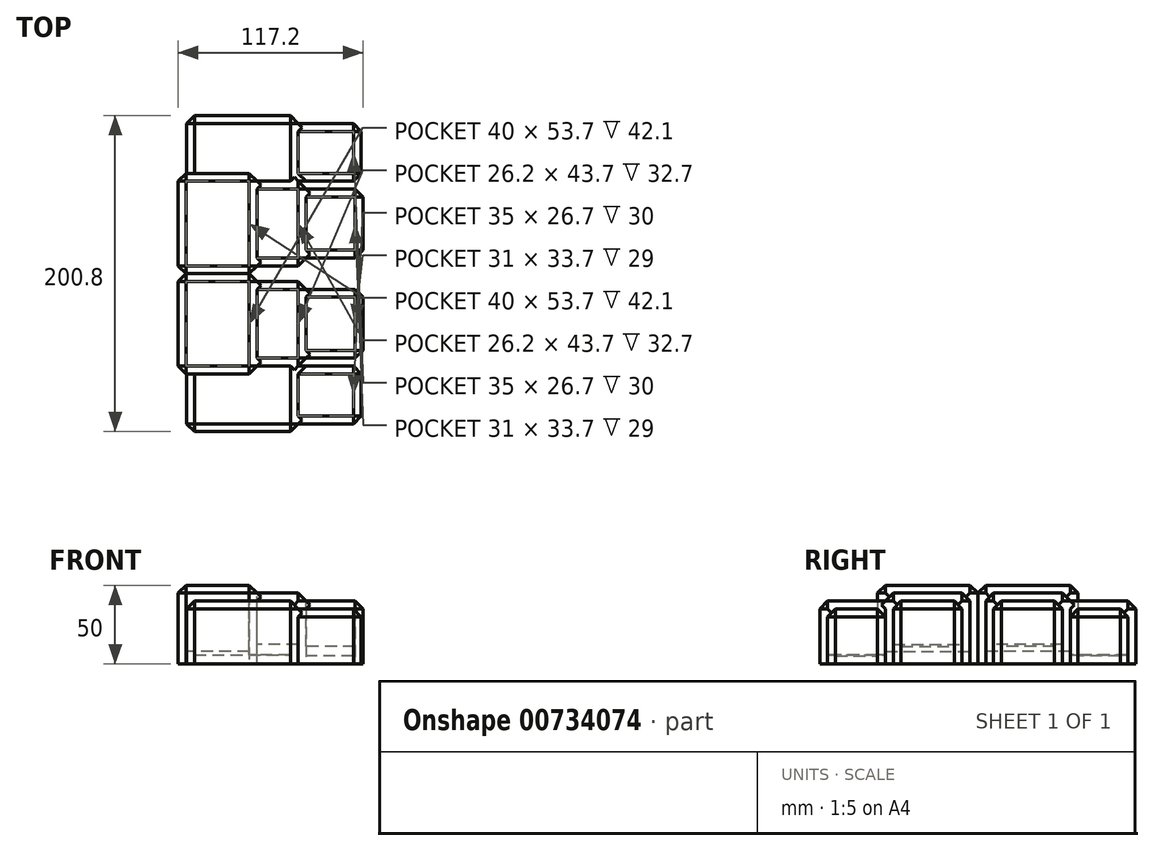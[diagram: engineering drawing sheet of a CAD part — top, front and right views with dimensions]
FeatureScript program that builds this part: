
annotation { "Feature Type Name" : "Feature", "Feature Type Description" : "" }
export const myFeature = defineFeature(function(context is Context, id is Id, definition is map)
    precondition{}
    {
        {
            var Q0;
            Q0=qCreatedBy(makeId("Front.planeOp"),FACE);
            var sketch = newSketch(context, id + "F0", { "sketchPlane" : qUnion([Q0])});
            skLineSegment(sketch, "E0.bottom", {"start": v(-30.12, 38) * mm, "end": v(19.88, 38) * mm});
            skLineSegment(sketch, "E0.top", {"start": v(-30.12, -12) * mm, "end": v(19.88, -12) * mm});
            skLineSegment(sketch, "E0.left", {"start": v(-30.12, 38) * mm, "end": v(-30.12, -12) * mm});
            skLineSegment(sketch, "E0.right", {"start": v(19.88, 38) * mm, "end": v(19.88, -12) * mm});
            skSolve(sketch);
        }
        {
            var Q0;
            Q0 = qSketchRegion(id + "F0", true);
            extrude(context, id + "F1", {"entities" : qUnion([Q0]), "depth" : 63.7 * mm, "offsetDistance" : 25 * mm});
        }
        {
            var Q0;
            Q0=makeQuery(id+"F1.opExtrude","CAP_EDGE",EDGE,{"disambiguationData":[OSD([sQuery(id+"F0.wireOp",EDGE,"E0.right")])],"isStart":false});
            var Q1;
            Q1=makeQuery(id+"F1.opExtrude","CAP_EDGE",EDGE,{"disambiguationData":[OSD([sQuery(id+"F0.wireOp",EDGE,"E0.bottom")])],"isStart":false});
            var Q2;
            Q2=makeQuery(id+"F1.opExtrude","CAP_EDGE",EDGE,{"disambiguationData":[OSD([sQuery(id+"F0.wireOp",EDGE,"E0.left")])],"isStart":false});
            var Q3;
            Q3=makeQuery(id+"F1.opExtrude","SWEPT_EDGE",EDGE,{"disambiguationData":[OSD([sQuery(id+"F0.wireOp",EDGE,"E0.bottom"),sQuery(id+"F0.wireOp",EDGE,"E0.right")])]});
            var Q4;
            Q4=makeQuery(id+"F1.opExtrude","SWEPT_EDGE",EDGE,{"disambiguationData":[OSD([sQuery(id+"F0.wireOp",EDGE,"E0.bottom"),sQuery(id+"F0.wireOp",EDGE,"E0.left")])]});
            var Q5;
            Q5=makeQuery(id+"F1.opExtrude","CAP_EDGE",EDGE,{"disambiguationData":[OSD([sQuery(id+"F0.wireOp",EDGE,"E0.right")])],"isStart":true});
            var Q6;
            Q6=makeQuery(id+"F1.opExtrude","CAP_EDGE",EDGE,{"disambiguationData":[OSD([sQuery(id+"F0.wireOp",EDGE,"E0.bottom")])],"isStart":true});
            var Q7;
            Q7=makeQuery(id+"F1.opExtrude","CAP_EDGE",EDGE,{"disambiguationData":[OSD([sQuery(id+"F0.wireOp",EDGE,"E0.left")])],"isStart":true});
            chamfer(context, id + "F2", {"entities" : qUnion([Q0, Q1, Q2, Q3, Q4, Q5, Q6, Q7]), "width" : 5 * mm, "tangentPropagation" : true});
        }
        {
            var Q0;
            Q0=makeQuery(id+"F1.opExtrude","SWEPT_FACE",FACE,{"disambiguationData":[OSD([sQuery(id+"F0.wireOp",EDGE,"E0.bottom")])]});
            extrude(context, id + "F3", {"entities" : qUnion([Q0]), "operationType" : NewBodyOperationType.REMOVE, "oppositeDirection" : true, "depth" : 42.1 * mm, "offsetDistance" : 25 * mm});
        }
        {
            var Q0;
            Q0=makeQuery(id+"F1.opExtrude","SWEPT_FACE",FACE,{"disambiguationData":[OSD([sQuery(id+"F0.wireOp",EDGE,"E0.right")])]});
            extrude(context, id + "F4", {"entities" : qUnion([Q0]), "operationType" : NewBodyOperationType.ADD, "depth" : 31.2 * mm, "offsetDistance" : 25 * mm});
        }
        {
            var Q0;
            {var subQ0=sQuery(id+"F0.wireOp",EDGE,"E0.right");var subQ1=sQuery(id+"F0.wireOp",EDGE,"E0.bottom");Q0=makeQuery(id+"F4.opExtrude","SWEPT_EDGE",EDGE,{"disambiguationData":[OSD([subQ1,subQ0]),TDD([makeQuery(id+"F2.opChamfer","BLEND_VERTEX",VERTEX,{"blendedFrom":[makeQuery(id+"F1.opExtrude","CAP_VERTEX",VERTEX,{"disambiguationData":[OSD([subQ1,subQ0])],"isStart":false}),makeQuery(id+"F1.opExtrude","SWEPT_EDGE",EDGE,{"disambiguationData":[OSD([subQ1,subQ0])]}),makeQuery(id+"F1.opExtrude","CAP_EDGE",EDGE,{"disambiguationData":[OSD([subQ0])],"isStart":false}),makeQuery(id+"F1.opExtrude","SWEPT_FACE",FACE,{"disambiguationData":[OSD([subQ0])]})],"blendedInto":[makeQuery(id+"F1.opExtrude","SWEPT_FACE",FACE,{"disambiguationData":[OSD([subQ0])]})]})])]});}
            var Q1;
            {var subQ0=sQuery(id+"F0.wireOp",EDGE,"E0.right");var subQ1=sQuery(id+"F0.wireOp",EDGE,"E0.bottom");Q1=makeQuery(id+"F4.opExtrude","SWEPT_EDGE",EDGE,{"disambiguationData":[OSD([subQ1,subQ0]),TDD([makeQuery(id+"F2.opChamfer","BLEND_VERTEX",VERTEX,{"blendedFrom":[makeQuery(id+"F1.opExtrude","CAP_VERTEX",VERTEX,{"disambiguationData":[OSD([subQ1,subQ0])],"isStart":true}),makeQuery(id+"F1.opExtrude","SWEPT_EDGE",EDGE,{"disambiguationData":[OSD([subQ1,subQ0])]}),makeQuery(id+"F1.opExtrude","CAP_EDGE",EDGE,{"disambiguationData":[OSD([subQ0])],"isStart":true}),makeQuery(id+"F1.opExtrude","SWEPT_FACE",FACE,{"disambiguationData":[OSD([subQ0])]})],"blendedInto":[makeQuery(id+"F1.opExtrude","SWEPT_FACE",FACE,{"disambiguationData":[OSD([subQ0])]})]})])]});}
            var Q2;
            Q2=makeQuery(id+"F4.opExtrude","CAP_EDGE",EDGE,{"disambiguationData":[OSD([sQuery(id+"F0.wireOp",EDGE,"E0.bottom"),sQuery(id+"F0.wireOp",EDGE,"E0.right")])],"isStart":false});
            var Q3;
            {var subQ0=sQuery(id+"F0.wireOp",EDGE,"E0.right");Q3=makeQuery(id+"F4.opExtrude","CAP_EDGE",EDGE,{"disambiguationData":[OSD([subQ0]),TDD([makeQuery(id+"F2.opChamfer","BLEND_EDGE",EDGE,{"blendedFrom":[makeQuery(id+"F1.opExtrude","CAP_EDGE",EDGE,{"disambiguationData":[OSD([subQ0])],"isStart":false}),makeQuery(id+"F1.opExtrude","SWEPT_FACE",FACE,{"disambiguationData":[OSD([subQ0])]})],"blendedInto":[makeQuery(id+"F1.opExtrude","SWEPT_FACE",FACE,{"disambiguationData":[OSD([subQ0])]})]})])],"isStart":false});}
            var Q4;
            {var subQ0=sQuery(id+"F0.wireOp",EDGE,"E0.right");Q4=makeQuery(id+"F4.opExtrude","CAP_EDGE",EDGE,{"disambiguationData":[OSD([subQ0]),TDD([makeQuery(id+"F2.opChamfer","BLEND_EDGE",EDGE,{"blendedFrom":[makeQuery(id+"F1.opExtrude","CAP_EDGE",EDGE,{"disambiguationData":[OSD([subQ0])],"isStart":true}),makeQuery(id+"F1.opExtrude","SWEPT_FACE",FACE,{"disambiguationData":[OSD([subQ0])]})],"blendedInto":[makeQuery(id+"F1.opExtrude","SWEPT_FACE",FACE,{"disambiguationData":[OSD([subQ0])]})]})])],"isStart":false});}
            chamfer(context, id + "F5", {"entities" : qUnion([Q0, Q1, Q2, Q3, Q4]), "width" : 5 * mm, "tangentPropagation" : true});
        }
        {
            var Q0;
            Q0=makeQuery(id+"F4.opExtrude","SWEPT_FACE",FACE,{"disambiguationData":[OSD([sQuery(id+"F0.wireOp",EDGE,"E0.bottom"),sQuery(id+"F0.wireOp",EDGE,"E0.right")])]});
            extrude(context, id + "F6", {"entities" : qUnion([Q0]), "operationType" : NewBodyOperationType.REMOVE, "oppositeDirection" : true, "depth" : 32.7 * mm, "offsetDistance" : 25 * mm});
        }
        {
            var Q0;
            {var subQ0=sQuery(id+"F0.wireOp",EDGE,"E0.right");Q0=makeQuery(id+"F4.opExtrude","SWEPT_FACE",FACE,{"disambiguationData":[OSD([subQ0]),TDD([makeQuery(id+"F2.opChamfer","BLEND_EDGE",EDGE,{"blendedFrom":[makeQuery(id+"F1.opExtrude","CAP_EDGE",EDGE,{"disambiguationData":[OSD([subQ0])],"isStart":false}),makeQuery(id+"F1.opExtrude","SWEPT_FACE",FACE,{"disambiguationData":[OSD([subQ0])]})],"blendedInto":[makeQuery(id+"F1.opExtrude","SWEPT_FACE",FACE,{"disambiguationData":[OSD([subQ0])]})]})])]});}
            extrude(context, id + "F7", {"entities" : qUnion([Q0]), "operationType" : NewBodyOperationType.ADD, "depth" : 41.7 * mm, "offsetDistance" : 25 * mm});
        }
        {
            var Q0;
            {var subQ0=sQuery(id+"F0.wireOp",EDGE,"E0.right");var subQ1=makeQuery(id+"F2.opChamfer","BLEND_EDGE",EDGE,{"blendedFrom":[makeQuery(id+"F1.opExtrude","CAP_EDGE",EDGE,{"disambiguationData":[OSD([subQ0])],"isStart":false}),makeQuery(id+"F1.opExtrude","SWEPT_FACE",FACE,{"disambiguationData":[OSD([subQ0])]})],"blendedInto":[makeQuery(id+"F1.opExtrude","SWEPT_FACE",FACE,{"disambiguationData":[OSD([subQ0])]})]});Q0=makeQuery(id+"F7.opExtrude","SWEPT_FACE",FACE,{"disambiguationData":[OSD([subQ0]),TDD([makeQuery(id+"F4.boolean.opBoolean","MERGE",EDGE,{"derivedFrom":[subQ1,makeQuery(id+"F4.opExtrude","CAP_EDGE",EDGE,{"disambiguationData":[OSD([subQ0]),TDD([subQ1])],"isStart":true})]})])]});}
            extrude(context, id + "F8", {"entities" : qUnion([Q0]), "operationType" : NewBodyOperationType.ADD, "depth" : 44.8 * mm, "offsetDistance" : 25 * mm});
        }
        {
            var Q0;
            Q0=makeQuery(id+"F8.opExtrude","CAP_EDGE",EDGE,{"disambiguationData":[OSD([sQuery(id+"F0.wireOp",EDGE,"E0.bottom"),sQuery(id+"F0.wireOp",EDGE,"E0.right")])],"isStart":false});
            var Q1;
            {var subQ0=sQuery(id+"F0.wireOp",EDGE,"E0.right");var subQ1=makeQuery(id+"F1.opExtrude","SWEPT_FACE",FACE,{"disambiguationData":[OSD([subQ0])]});var subQ2=makeQuery(id+"F1.opExtrude","CAP_EDGE",EDGE,{"disambiguationData":[OSD([subQ0])],"isStart":false});var subQ3=sQuery(id+"F0.wireOp",EDGE,"E0.bottom");Q1=makeQuery(id+"F8.boolean.opBoolean","MERGE",EDGE,{"derivedFrom":[makeQuery(id+"F7.opExtrude","CAP_EDGE",EDGE,{"disambiguationData":[OSD([subQ3,subQ0])],"isStart":false}),makeQuery(id+"F8.opExtrude","SWEPT_EDGE",EDGE,{"disambiguationData":[OSD([subQ3,subQ0]),TDD([makeQuery(id+"F7.opExtrude","CAP_VERTEX",VERTEX,{"disambiguationData":[OSD([subQ3,subQ0]),TDD([makeQuery(id+"F5.opChamfer","BLEND_VERTEX",VERTEX,{"blendedFrom":[makeQuery(id+"F4.opExtrude","SWEPT_EDGE",EDGE,{"disambiguationData":[OSD([subQ3,subQ0]),TDD([makeQuery(id+"F2.opChamfer","BLEND_VERTEX",VERTEX,{"blendedFrom":[makeQuery(id+"F1.opExtrude","CAP_VERTEX",VERTEX,{"disambiguationData":[OSD([subQ3,subQ0])],"isStart":false}),makeQuery(id+"F1.opExtrude","SWEPT_EDGE",EDGE,{"disambiguationData":[OSD([subQ3,subQ0])]}),subQ2,subQ1],"blendedInto":[subQ1]})])]}),makeQuery(id+"F2.opChamfer","BLEND_FACE",FACE,{"disambiguationData":[OSD([subQ0]),TDD([subQ2])]}),makeQuery(id+"F4.opExtrude","SWEPT_FACE",FACE,{"disambiguationData":[OSD([subQ0]),TDD([makeQuery(id+"F2.opChamfer","BLEND_EDGE",EDGE,{"blendedFrom":[subQ2,subQ1],"blendedInto":[subQ1]})])]})],"blendedInto":[makeQuery(id+"F2.opChamfer","BLEND_FACE",FACE,{"disambiguationData":[OSD([subQ0]),TDD([subQ2])]}),makeQuery(id+"F4.opExtrude","SWEPT_FACE",FACE,{"disambiguationData":[OSD([subQ0]),TDD([makeQuery(id+"F2.opChamfer","BLEND_EDGE",EDGE,{"blendedFrom":[subQ2,subQ1],"blendedInto":[subQ1]})])]})]})])],"isStart":false})])]})]});}
            var Q2;
            {var subQ0=sQuery(id+"F0.wireOp",EDGE,"E0.right");var subQ1=makeQuery(id+"F1.opExtrude","SWEPT_FACE",FACE,{"disambiguationData":[OSD([subQ0])]});var subQ2=makeQuery(id+"F1.opExtrude","CAP_EDGE",EDGE,{"disambiguationData":[OSD([subQ0])],"isStart":false});var subQ3=makeQuery(id+"F2.opChamfer","BLEND_EDGE",EDGE,{"blendedFrom":[subQ2,subQ1],"blendedInto":[subQ1]});var subQ4=sQuery(id+"F0.wireOp",EDGE,"E0.bottom");var subQ5=makeQuery(id+"F2.opChamfer","BLEND_VERTEX",VERTEX,{"blendedFrom":[makeQuery(id+"F1.opExtrude","CAP_VERTEX",VERTEX,{"disambiguationData":[OSD([subQ4,subQ0])],"isStart":false}),makeQuery(id+"F1.opExtrude","SWEPT_EDGE",EDGE,{"disambiguationData":[OSD([subQ4,subQ0])]}),subQ2,subQ1],"blendedInto":[subQ1]});Q2=makeQuery(id+"F7.opExtrude","SWEPT_EDGE",EDGE,{"disambiguationData":[OSD([subQ4,subQ0]),TDD([makeQuery(id+"F5.opChamfer","BLEND_VERTEX",VERTEX,{"blendedFrom":[makeQuery(id+"F4.opExtrude","CAP_VERTEX",VERTEX,{"disambiguationData":[OSD([subQ4,subQ0]),TDD([subQ5])],"isStart":false}),makeQuery(id+"F4.opExtrude","SWEPT_EDGE",EDGE,{"disambiguationData":[OSD([subQ4,subQ0]),TDD([subQ5])]}),makeQuery(id+"F4.opExtrude","CAP_EDGE",EDGE,{"disambiguationData":[OSD([subQ0]),TDD([subQ3])],"isStart":false}),makeQuery(id+"F4.opExtrude","SWEPT_FACE",FACE,{"disambiguationData":[OSD([subQ0]),TDD([subQ3])]})],"blendedInto":[makeQuery(id+"F4.opExtrude","SWEPT_FACE",FACE,{"disambiguationData":[OSD([subQ0]),TDD([subQ3])]})]})])]});}
            var Q3;
            {var subQ0=sQuery(id+"F0.wireOp",EDGE,"E0.right");var subQ1=makeQuery(id+"F2.opChamfer","BLEND_EDGE",EDGE,{"blendedFrom":[makeQuery(id+"F1.opExtrude","CAP_EDGE",EDGE,{"disambiguationData":[OSD([subQ0])],"isStart":false}),makeQuery(id+"F1.opExtrude","SWEPT_FACE",FACE,{"disambiguationData":[OSD([subQ0])]})],"blendedInto":[makeQuery(id+"F1.opExtrude","SWEPT_FACE",FACE,{"disambiguationData":[OSD([subQ0])]})]});Q3=makeQuery(id+"F7.opExtrude","CAP_EDGE",EDGE,{"disambiguationData":[OSD([subQ0]),TDD([makeQuery(id+"F5.opChamfer","BLEND_EDGE",EDGE,{"blendedFrom":[makeQuery(id+"F4.opExtrude","CAP_EDGE",EDGE,{"disambiguationData":[OSD([subQ0]),TDD([subQ1])],"isStart":false}),makeQuery(id+"F4.opExtrude","SWEPT_FACE",FACE,{"disambiguationData":[OSD([subQ0]),TDD([subQ1])]})],"blendedInto":[makeQuery(id+"F4.opExtrude","SWEPT_FACE",FACE,{"disambiguationData":[OSD([subQ0]),TDD([subQ1])]})]})])],"isStart":false});}
            var Q4;
            {var subQ0=sQuery(id+"F0.wireOp",EDGE,"E0.right");var subQ1=makeQuery(id+"F2.opChamfer","BLEND_EDGE",EDGE,{"blendedFrom":[makeQuery(id+"F1.opExtrude","CAP_EDGE",EDGE,{"disambiguationData":[OSD([subQ0])],"isStart":false}),makeQuery(id+"F1.opExtrude","SWEPT_FACE",FACE,{"disambiguationData":[OSD([subQ0])]})],"blendedInto":[makeQuery(id+"F1.opExtrude","SWEPT_FACE",FACE,{"disambiguationData":[OSD([subQ0])]})]});Q4=makeQuery(id+"F8.opExtrude","CAP_EDGE",EDGE,{"disambiguationData":[OSD([subQ0]),TDD([makeQuery(id+"F7.opExtrude","CAP_EDGE",EDGE,{"disambiguationData":[OSD([subQ0]),TDD([makeQuery(id+"F4.boolean.opBoolean","MERGE",EDGE,{"derivedFrom":[subQ1,makeQuery(id+"F4.opExtrude","CAP_EDGE",EDGE,{"disambiguationData":[OSD([subQ0]),TDD([subQ1])],"isStart":true})]})])],"isStart":false})])],"isStart":false});}
            chamfer(context, id + "F9", {"entities" : qUnion([Q0, Q1, Q2, Q3, Q4]), "width" : 5 * mm, "tangentPropagation" : true});
        }
        {
            var Q0;
            {var subQ0=sQuery(id+"F0.wireOp",EDGE,"E0.right");var subQ1=sQuery(id+"F0.wireOp",EDGE,"E0.bottom");Q0=makeQuery(id+"F8.boolean.opBoolean","MERGE",FACE,{"derivedFrom":[makeQuery(id+"F7.opExtrude","SWEPT_FACE",FACE,{"disambiguationData":[OSD([subQ1,subQ0])]}),makeQuery(id+"F8.opExtrude","SWEPT_FACE",FACE,{"disambiguationData":[OSD([subQ1,subQ0])]})]});}
            extrude(context, id + "F10", {"entities" : qUnion([Q0]), "operationType" : NewBodyOperationType.REMOVE, "oppositeDirection" : true, "depth" : 34.3 * mm, "offsetDistance" : 25 * mm});
        }
        {
            var Q0;
            {var subQ0=sQuery(id+"F0.wireOp",EDGE,"E0.right");var subQ1=makeQuery(id+"F2.opChamfer","BLEND_EDGE",EDGE,{"blendedFrom":[makeQuery(id+"F1.opExtrude","CAP_EDGE",EDGE,{"disambiguationData":[OSD([subQ0])],"isStart":false}),makeQuery(id+"F1.opExtrude","SWEPT_FACE",FACE,{"disambiguationData":[OSD([subQ0])]})],"blendedInto":[makeQuery(id+"F1.opExtrude","SWEPT_FACE",FACE,{"disambiguationData":[OSD([subQ0])]})]});Q0=makeQuery(id+"F7.opExtrude","SWEPT_FACE",FACE,{"disambiguationData":[OSD([subQ0]),TDD([makeQuery(id+"F5.opChamfer","BLEND_EDGE",EDGE,{"blendedFrom":[makeQuery(id+"F4.opExtrude","CAP_EDGE",EDGE,{"disambiguationData":[OSD([subQ0]),TDD([subQ1])],"isStart":false}),makeQuery(id+"F4.opExtrude","SWEPT_FACE",FACE,{"disambiguationData":[OSD([subQ0]),TDD([subQ1])]})],"blendedInto":[makeQuery(id+"F4.opExtrude","SWEPT_FACE",FACE,{"disambiguationData":[OSD([subQ0]),TDD([subQ1])]})]})])]});}
            extrude(context, id + "F11", {"entities" : qUnion([Q0]), "operationType" : NewBodyOperationType.ADD, "depth" : 40 * mm, "offsetDistance" : 25 * mm});
        }
        {
            var Q0;
            {var subQ0=sQuery(id+"F0.wireOp",EDGE,"E0.right");var subQ1=makeQuery(id+"F1.opExtrude","SWEPT_FACE",FACE,{"disambiguationData":[OSD([subQ0])]});var subQ2=makeQuery(id+"F1.opExtrude","CAP_EDGE",EDGE,{"disambiguationData":[OSD([subQ0])],"isStart":false});var subQ3=makeQuery(id+"F2.opChamfer","BLEND_EDGE",EDGE,{"blendedFrom":[subQ2,subQ1],"blendedInto":[subQ1]});var subQ4=makeQuery(id+"F4.opExtrude","SWEPT_FACE",FACE,{"disambiguationData":[OSD([subQ0]),TDD([subQ3])]});var subQ5=makeQuery(id+"F4.opExtrude","CAP_EDGE",EDGE,{"disambiguationData":[OSD([subQ0]),TDD([subQ3])],"isStart":false});var subQ6=makeQuery(id+"F5.opChamfer","BLEND_EDGE",EDGE,{"blendedFrom":[subQ5,subQ4],"blendedInto":[subQ4]});var subQ7=sQuery(id+"F0.wireOp",EDGE,"E0.bottom");var subQ8=makeQuery(id+"F2.opChamfer","BLEND_VERTEX",VERTEX,{"blendedFrom":[makeQuery(id+"F1.opExtrude","CAP_VERTEX",VERTEX,{"disambiguationData":[OSD([subQ7,subQ0])],"isStart":false}),makeQuery(id+"F1.opExtrude","SWEPT_EDGE",EDGE,{"disambiguationData":[OSD([subQ7,subQ0])]}),subQ2,subQ1],"blendedInto":[subQ1]});var subQ9=makeQuery(id+"F5.opChamfer","BLEND_VERTEX",VERTEX,{"blendedFrom":[makeQuery(id+"F4.opExtrude","CAP_VERTEX",VERTEX,{"disambiguationData":[OSD([subQ7,subQ0]),TDD([subQ8])],"isStart":false}),makeQuery(id+"F4.opExtrude","SWEPT_EDGE",EDGE,{"disambiguationData":[OSD([subQ7,subQ0]),TDD([subQ8])]}),subQ5,subQ4],"blendedInto":[subQ4]});Q0=makeQuery(id+"F11.opExtrude","SWEPT_EDGE",EDGE,{"disambiguationData":[OSD([subQ7,subQ0]),TDD([makeQuery(id+"F9.opChamfer","BLEND_VERTEX",VERTEX,{"blendedFrom":[makeQuery(id+"F7.opExtrude","CAP_VERTEX",VERTEX,{"disambiguationData":[OSD([subQ7,subQ0]),TDD([subQ9])],"isStart":false}),makeQuery(id+"F7.opExtrude","SWEPT_EDGE",EDGE,{"disambiguationData":[OSD([subQ7,subQ0]),TDD([subQ9])]}),makeQuery(id+"F7.opExtrude","CAP_EDGE",EDGE,{"disambiguationData":[OSD([subQ0]),TDD([subQ6])],"isStart":false}),makeQuery(id+"F7.opExtrude","SWEPT_FACE",FACE,{"disambiguationData":[OSD([subQ0]),TDD([subQ6])]})],"blendedInto":[makeQuery(id+"F7.opExtrude","SWEPT_FACE",FACE,{"disambiguationData":[OSD([subQ0]),TDD([subQ6])]})]})])]});}
            var Q1;
            {var subQ0=sQuery(id+"F0.wireOp",EDGE,"E0.right");var subQ1=makeQuery(id+"F2.opChamfer","BLEND_EDGE",EDGE,{"blendedFrom":[makeQuery(id+"F1.opExtrude","CAP_EDGE",EDGE,{"disambiguationData":[OSD([subQ0])],"isStart":false}),makeQuery(id+"F1.opExtrude","SWEPT_FACE",FACE,{"disambiguationData":[OSD([subQ0])]})],"blendedInto":[makeQuery(id+"F1.opExtrude","SWEPT_FACE",FACE,{"disambiguationData":[OSD([subQ0])]})]});var subQ2=makeQuery(id+"F5.opChamfer","BLEND_EDGE",EDGE,{"blendedFrom":[makeQuery(id+"F4.opExtrude","CAP_EDGE",EDGE,{"disambiguationData":[OSD([subQ0]),TDD([subQ1])],"isStart":false}),makeQuery(id+"F4.opExtrude","SWEPT_FACE",FACE,{"disambiguationData":[OSD([subQ0]),TDD([subQ1])]})],"blendedInto":[makeQuery(id+"F4.opExtrude","SWEPT_FACE",FACE,{"disambiguationData":[OSD([subQ0]),TDD([subQ1])]})]});Q1=makeQuery(id+"F11.opExtrude","CAP_EDGE",EDGE,{"disambiguationData":[OSD([subQ0]),TDD([makeQuery(id+"F9.opChamfer","BLEND_EDGE",EDGE,{"blendedFrom":[makeQuery(id+"F7.opExtrude","CAP_EDGE",EDGE,{"disambiguationData":[OSD([subQ0]),TDD([subQ2])],"isStart":false}),makeQuery(id+"F7.opExtrude","SWEPT_FACE",FACE,{"disambiguationData":[OSD([subQ0]),TDD([subQ2])]})],"blendedInto":[makeQuery(id+"F7.opExtrude","SWEPT_FACE",FACE,{"disambiguationData":[OSD([subQ0]),TDD([subQ2])]})]})])],"isStart":false});}
            var Q2;
            {var subQ0=sQuery(id+"F0.wireOp",EDGE,"E0.right");var subQ1=makeQuery(id+"F2.opChamfer","BLEND_EDGE",EDGE,{"blendedFrom":[makeQuery(id+"F1.opExtrude","CAP_EDGE",EDGE,{"disambiguationData":[OSD([subQ0])],"isStart":false}),makeQuery(id+"F1.opExtrude","SWEPT_FACE",FACE,{"disambiguationData":[OSD([subQ0])]})],"blendedInto":[makeQuery(id+"F1.opExtrude","SWEPT_FACE",FACE,{"disambiguationData":[OSD([subQ0])]})]});var subQ2=makeQuery(id+"F5.opChamfer","BLEND_EDGE",EDGE,{"blendedFrom":[makeQuery(id+"F4.opExtrude","CAP_EDGE",EDGE,{"disambiguationData":[OSD([subQ0]),TDD([subQ1])],"isStart":false}),makeQuery(id+"F4.opExtrude","SWEPT_FACE",FACE,{"disambiguationData":[OSD([subQ0]),TDD([subQ1])]})],"blendedInto":[makeQuery(id+"F4.opExtrude","SWEPT_FACE",FACE,{"disambiguationData":[OSD([subQ0]),TDD([subQ1])]})]});Q2=makeQuery(id+"F11.opExtrude","CAP_EDGE",EDGE,{"disambiguationData":[OSD([subQ0]),TDD([makeQuery(id+"F7.boolean.opBoolean","MERGE",EDGE,{"derivedFrom":[subQ2,makeQuery(id+"F7.opExtrude","CAP_EDGE",EDGE,{"disambiguationData":[OSD([subQ0]),TDD([subQ2])],"isStart":true})]})])],"isStart":false});}
            var Q3;
            {var subQ0=sQuery(id+"F0.wireOp",EDGE,"E0.right");var subQ1=makeQuery(id+"F1.opExtrude","SWEPT_FACE",FACE,{"disambiguationData":[OSD([subQ0])]});var subQ2=makeQuery(id+"F1.opExtrude","CAP_EDGE",EDGE,{"disambiguationData":[OSD([subQ0])],"isStart":false});var subQ3=makeQuery(id+"F2.opChamfer","BLEND_EDGE",EDGE,{"blendedFrom":[subQ2,subQ1],"blendedInto":[subQ1]});var subQ4=makeQuery(id+"F4.opExtrude","SWEPT_FACE",FACE,{"disambiguationData":[OSD([subQ0]),TDD([subQ3])]});var subQ5=makeQuery(id+"F4.opExtrude","CAP_EDGE",EDGE,{"disambiguationData":[OSD([subQ0]),TDD([subQ3])],"isStart":false});var subQ6=sQuery(id+"F0.wireOp",EDGE,"E0.bottom");var subQ7=makeQuery(id+"F2.opChamfer","BLEND_VERTEX",VERTEX,{"blendedFrom":[makeQuery(id+"F1.opExtrude","CAP_VERTEX",VERTEX,{"disambiguationData":[OSD([subQ6,subQ0])],"isStart":false}),makeQuery(id+"F1.opExtrude","SWEPT_EDGE",EDGE,{"disambiguationData":[OSD([subQ6,subQ0])]}),subQ2,subQ1],"blendedInto":[subQ1]});Q3=makeQuery(id+"F11.opExtrude","SWEPT_EDGE",EDGE,{"disambiguationData":[OSD([subQ6,subQ0]),TDD([makeQuery(id+"F9.opChamfer","BLEND_VERTEX",VERTEX,{"blendedFrom":[makeQuery(id+"F7.opExtrude","SWEPT_EDGE",EDGE,{"disambiguationData":[OSD([subQ6,subQ0]),TDD([makeQuery(id+"F5.opChamfer","BLEND_VERTEX",VERTEX,{"blendedFrom":[makeQuery(id+"F4.opExtrude","CAP_VERTEX",VERTEX,{"disambiguationData":[OSD([subQ6,subQ0]),TDD([subQ7])],"isStart":false}),makeQuery(id+"F4.opExtrude","SWEPT_EDGE",EDGE,{"disambiguationData":[OSD([subQ6,subQ0]),TDD([subQ7])]}),subQ5,subQ4],"blendedInto":[subQ4]})])]}),makeQuery(id+"F5.opChamfer","BLEND_FACE",FACE,{"disambiguationData":[OSD([subQ0]),TDD([subQ5])]}),makeQuery(id+"F7.opExtrude","SWEPT_FACE",FACE,{"disambiguationData":[OSD([subQ0]),TDD([makeQuery(id+"F5.opChamfer","BLEND_EDGE",EDGE,{"blendedFrom":[subQ5,subQ4],"blendedInto":[subQ4]})])]})],"blendedInto":[makeQuery(id+"F5.opChamfer","BLEND_FACE",FACE,{"disambiguationData":[OSD([subQ0]),TDD([subQ5])]}),makeQuery(id+"F7.opExtrude","SWEPT_FACE",FACE,{"disambiguationData":[OSD([subQ0]),TDD([makeQuery(id+"F5.opChamfer","BLEND_EDGE",EDGE,{"blendedFrom":[subQ5,subQ4],"blendedInto":[subQ4]})])]})]})])]});}
            var Q4;
            Q4=makeQuery(id+"F11.opExtrude","CAP_EDGE",EDGE,{"disambiguationData":[OSD([sQuery(id+"F0.wireOp",EDGE,"E0.bottom"),sQuery(id+"F0.wireOp",EDGE,"E0.right")])],"isStart":false});
            chamfer(context, id + "F12", {"entities" : qUnion([Q0, Q1, Q2, Q3, Q4]), "width" : 5 * mm, "tangentPropagation" : true});
        }
        {
            var Q0;
            Q0=makeQuery(id+"F11.opExtrude","SWEPT_FACE",FACE,{"disambiguationData":[OSD([sQuery(id+"F0.wireOp",EDGE,"E0.bottom"),sQuery(id+"F0.wireOp",EDGE,"E0.right")])]});
            extrude(context, id + "F13", {"entities" : qUnion([Q0]), "operationType" : NewBodyOperationType.REMOVE, "oppositeDirection" : true, "depth" : 30 * mm, "offsetDistance" : 25 * mm});
        }
        {
            var Q0;
            Q0=makeQuery(id+"F4.opExtrude","CAP_FACE",FACE,{"disambiguationData":[OSD([sQuery(id+"F0.wireOp",EDGE,"E0.right")])],"isStart":false});
            extrude(context, id + "F14", {"entities" : qUnion([Q0]), "operationType" : NewBodyOperationType.ADD, "depth" : 36 * mm, "offsetDistance" : 25 * mm});
        }
        {
            var Q0;
            {var subQ0=sQuery(id+"F0.wireOp",EDGE,"E0.right");var subQ1=makeQuery(id+"F1.opExtrude","SWEPT_FACE",FACE,{"disambiguationData":[OSD([subQ0])]});var subQ2=makeQuery(id+"F1.opExtrude","CAP_EDGE",EDGE,{"disambiguationData":[OSD([subQ0])],"isStart":false});var subQ3=sQuery(id+"F0.wireOp",EDGE,"E0.bottom");Q0=makeQuery(id+"F14.opExtrude","SWEPT_EDGE",EDGE,{"disambiguationData":[OSD([subQ3,subQ0]),TDD([makeQuery(id+"F5.opChamfer","BLEND_VERTEX",VERTEX,{"blendedFrom":[makeQuery(id+"F4.opExtrude","CAP_VERTEX",VERTEX,{"disambiguationData":[OSD([subQ3,subQ0]),TDD([makeQuery(id+"F2.opChamfer","BLEND_VERTEX",VERTEX,{"blendedFrom":[makeQuery(id+"F1.opExtrude","CAP_VERTEX",VERTEX,{"disambiguationData":[OSD([subQ3,subQ0])],"isStart":false}),makeQuery(id+"F1.opExtrude","SWEPT_EDGE",EDGE,{"disambiguationData":[OSD([subQ3,subQ0])]}),subQ2,subQ1],"blendedInto":[subQ1]})])],"isStart":false}),makeQuery(id+"F4.opExtrude","CAP_EDGE",EDGE,{"disambiguationData":[OSD([subQ3,subQ0])],"isStart":false}),makeQuery(id+"F4.opExtrude","CAP_EDGE",EDGE,{"disambiguationData":[OSD([subQ0]),TDD([makeQuery(id+"F2.opChamfer","BLEND_EDGE",EDGE,{"blendedFrom":[subQ2,subQ1],"blendedInto":[subQ1]})])],"isStart":false}),makeQuery(id+"F4.opExtrude","CAP_FACE",FACE,{"disambiguationData":[OSD([subQ0])],"isStart":false})],"blendedInto":[makeQuery(id+"F4.opExtrude","CAP_FACE",FACE,{"disambiguationData":[OSD([subQ0])],"isStart":false})]})])]});}
            var Q1;
            {var subQ0=sQuery(id+"F0.wireOp",EDGE,"E0.right");Q1=makeQuery(id+"F14.opExtrude","CAP_EDGE",EDGE,{"disambiguationData":[OSD([subQ0]),TDD([makeQuery(id+"F5.opChamfer","BLEND_EDGE",EDGE,{"blendedFrom":[makeQuery(id+"F4.opExtrude","CAP_EDGE",EDGE,{"disambiguationData":[OSD([subQ0]),TDD([makeQuery(id+"F2.opChamfer","BLEND_EDGE",EDGE,{"blendedFrom":[makeQuery(id+"F1.opExtrude","CAP_EDGE",EDGE,{"disambiguationData":[OSD([subQ0])],"isStart":false}),makeQuery(id+"F1.opExtrude","SWEPT_FACE",FACE,{"disambiguationData":[OSD([subQ0])]})],"blendedInto":[makeQuery(id+"F1.opExtrude","SWEPT_FACE",FACE,{"disambiguationData":[OSD([subQ0])]})]})])],"isStart":false}),makeQuery(id+"F4.opExtrude","CAP_FACE",FACE,{"disambiguationData":[OSD([subQ0])],"isStart":false})],"blendedInto":[makeQuery(id+"F4.opExtrude","CAP_FACE",FACE,{"disambiguationData":[OSD([subQ0])],"isStart":false})]})])],"isStart":false});}
            var Q2;
            {var subQ0=sQuery(id+"F0.wireOp",EDGE,"E0.right");var subQ1=makeQuery(id+"F1.opExtrude","SWEPT_FACE",FACE,{"disambiguationData":[OSD([subQ0])]});var subQ2=makeQuery(id+"F1.opExtrude","CAP_EDGE",EDGE,{"disambiguationData":[OSD([subQ0])],"isStart":true});var subQ3=sQuery(id+"F0.wireOp",EDGE,"E0.bottom");Q2=makeQuery(id+"F14.opExtrude","SWEPT_EDGE",EDGE,{"disambiguationData":[OSD([subQ3,subQ0]),TDD([makeQuery(id+"F5.opChamfer","BLEND_VERTEX",VERTEX,{"blendedFrom":[makeQuery(id+"F4.opExtrude","CAP_VERTEX",VERTEX,{"disambiguationData":[OSD([subQ3,subQ0]),TDD([makeQuery(id+"F2.opChamfer","BLEND_VERTEX",VERTEX,{"blendedFrom":[makeQuery(id+"F1.opExtrude","CAP_VERTEX",VERTEX,{"disambiguationData":[OSD([subQ3,subQ0])],"isStart":true}),makeQuery(id+"F1.opExtrude","SWEPT_EDGE",EDGE,{"disambiguationData":[OSD([subQ3,subQ0])]}),subQ2,subQ1],"blendedInto":[subQ1]})])],"isStart":false}),makeQuery(id+"F4.opExtrude","CAP_EDGE",EDGE,{"disambiguationData":[OSD([subQ3,subQ0])],"isStart":false}),makeQuery(id+"F4.opExtrude","CAP_EDGE",EDGE,{"disambiguationData":[OSD([subQ0]),TDD([makeQuery(id+"F2.opChamfer","BLEND_EDGE",EDGE,{"blendedFrom":[subQ2,subQ1],"blendedInto":[subQ1]})])],"isStart":false}),makeQuery(id+"F4.opExtrude","CAP_FACE",FACE,{"disambiguationData":[OSD([subQ0])],"isStart":false})],"blendedInto":[makeQuery(id+"F4.opExtrude","CAP_FACE",FACE,{"disambiguationData":[OSD([subQ0])],"isStart":false})]})])]});}
            var Q3;
            Q3=makeQuery(id+"F14.opExtrude","CAP_EDGE",EDGE,{"disambiguationData":[OSD([sQuery(id+"F0.wireOp",EDGE,"E0.bottom"),sQuery(id+"F0.wireOp",EDGE,"E0.right")])],"isStart":false});
            var Q4;
            {var subQ0=sQuery(id+"F0.wireOp",EDGE,"E0.right");Q4=makeQuery(id+"F14.opExtrude","CAP_EDGE",EDGE,{"disambiguationData":[OSD([subQ0]),TDD([makeQuery(id+"F5.opChamfer","BLEND_EDGE",EDGE,{"blendedFrom":[makeQuery(id+"F4.opExtrude","CAP_EDGE",EDGE,{"disambiguationData":[OSD([subQ0]),TDD([makeQuery(id+"F2.opChamfer","BLEND_EDGE",EDGE,{"blendedFrom":[makeQuery(id+"F1.opExtrude","CAP_EDGE",EDGE,{"disambiguationData":[OSD([subQ0])],"isStart":true}),makeQuery(id+"F1.opExtrude","SWEPT_FACE",FACE,{"disambiguationData":[OSD([subQ0])]})],"blendedInto":[makeQuery(id+"F1.opExtrude","SWEPT_FACE",FACE,{"disambiguationData":[OSD([subQ0])]})]})])],"isStart":false}),makeQuery(id+"F4.opExtrude","CAP_FACE",FACE,{"disambiguationData":[OSD([subQ0])],"isStart":false})],"blendedInto":[makeQuery(id+"F4.opExtrude","CAP_FACE",FACE,{"disambiguationData":[OSD([subQ0])],"isStart":false})]})])],"isStart":false});}
            chamfer(context, id + "F15", {"entities" : qUnion([Q0, Q1, Q2, Q3, Q4]), "width" : 5 * mm, "tangentPropagation" : true});
        }
        {
            var Q0;
            Q0=makeQuery(id+"F14.opExtrude","SWEPT_FACE",FACE,{"disambiguationData":[OSD([sQuery(id+"F0.wireOp",EDGE,"E0.bottom"),sQuery(id+"F0.wireOp",EDGE,"E0.right")])]});
            extrude(context, id + "F16", {"entities" : qUnion([Q0]), "operationType" : NewBodyOperationType.REMOVE, "oppositeDirection" : true, "depth" : 29 * mm, "offsetDistance" : 25 * mm});
        }
        {
            var Q0;
            Q0=makeQuery(id+"F1.opExtrude","SWEPT_BODY",BODY,{"disambiguationData":[OSD([sQuery(id+"F0.wireOp",EDGE,"E0.bottom"),sQuery(id+"F0.wireOp",EDGE,"E0.top"),sQuery(id+"F0.wireOp",EDGE,"E0.left"),sQuery(id+"F0.wireOp",EDGE,"E0.right")])]});
            var Q1;
            Q1=qCreatedBy(makeId("Front.planeOp"),FACE);
            mirror(context, id + "F17", {"operationType" : NewBodyOperationType.ADD, "entities" : qUnion([Q0]), "mirrorPlane" : qUnion([Q1])});
        }
    });
